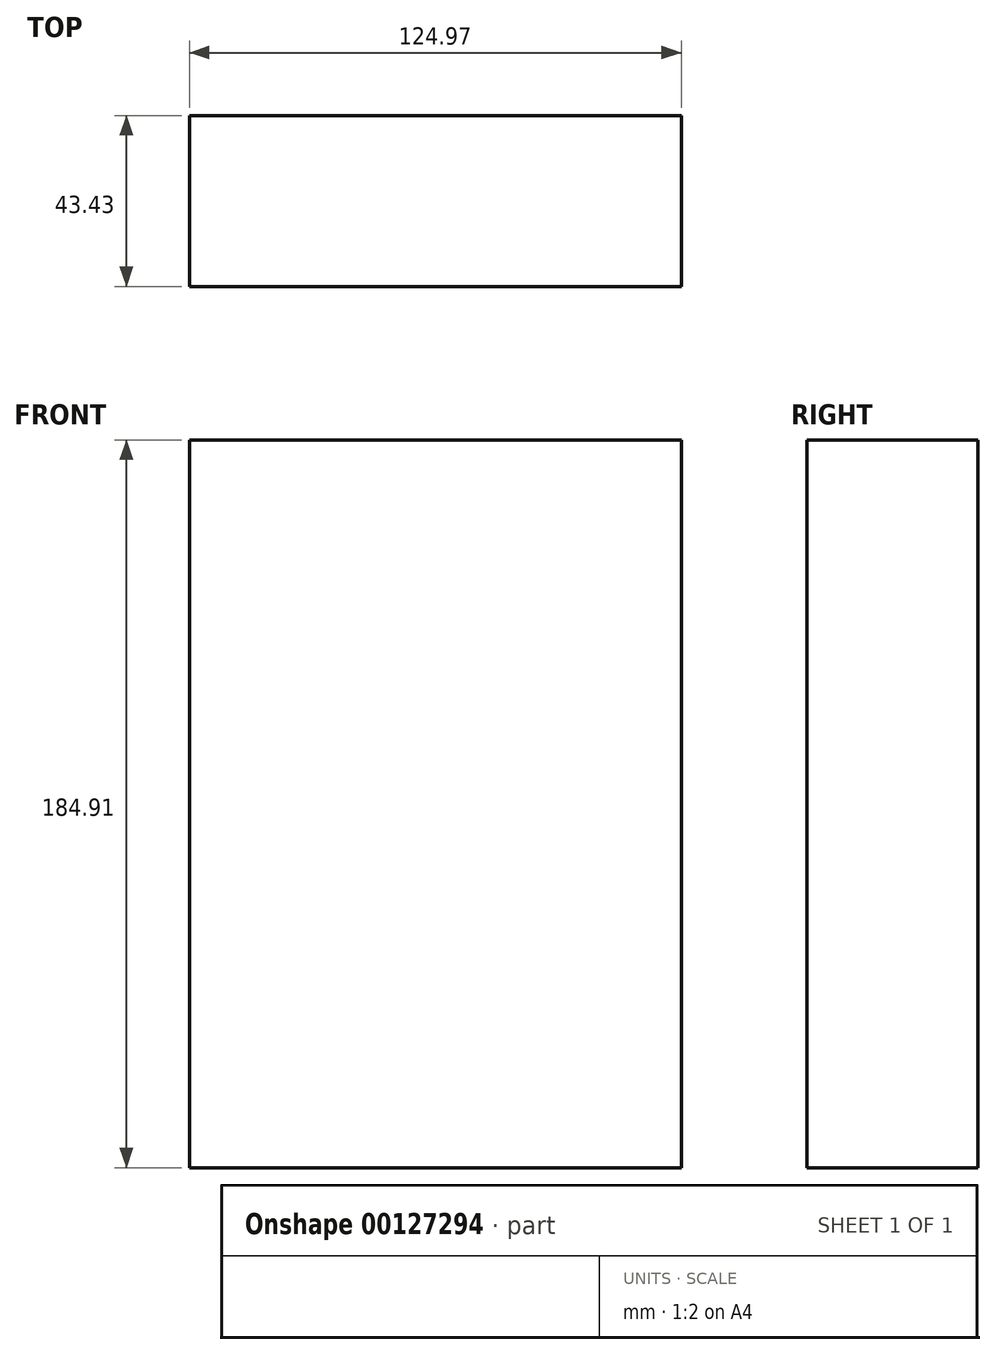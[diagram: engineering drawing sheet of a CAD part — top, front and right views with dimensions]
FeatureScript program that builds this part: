
annotation { "Feature Type Name" : "Feature", "Feature Type Description" : "" }
export const myFeature = defineFeature(function(context is Context, id is Id, definition is map)
    precondition{}
    {
        {
            var Q0;
            Q0=qCreatedBy(makeId("Front.planeOp"),FACE);
            var sketch = newSketch(context, id + "F0", { "sketchPlane" : qUnion([Q0])});
            skLineSegment(sketch, "E0", {"start": v(-99.46, 95.14) * mm, "end": v(-99.46, -89.77) * mm});
            skLineSegment(sketch, "E1", {"start": v(-99.46, -89.77) * mm, "end": v(25.51, -89.77) * mm});
            skLineSegment(sketch, "E2", {"start": v(25.51, -89.77) * mm, "end": v(25.51, 95.14) * mm});
            skLineSegment(sketch, "E3", {"start": v(25.51, 95.14) * mm, "end": v(-99.46, 95.14) * mm});
            skSolve(sketch);
        }
        {
            var Q0;
            Q0 = qSketchRegion(id + "F0", true);
            extrude(context, id + "F1", {"entities" : qUnion([Q0]), "depth" : 43.43 * mm});
        }
    });
